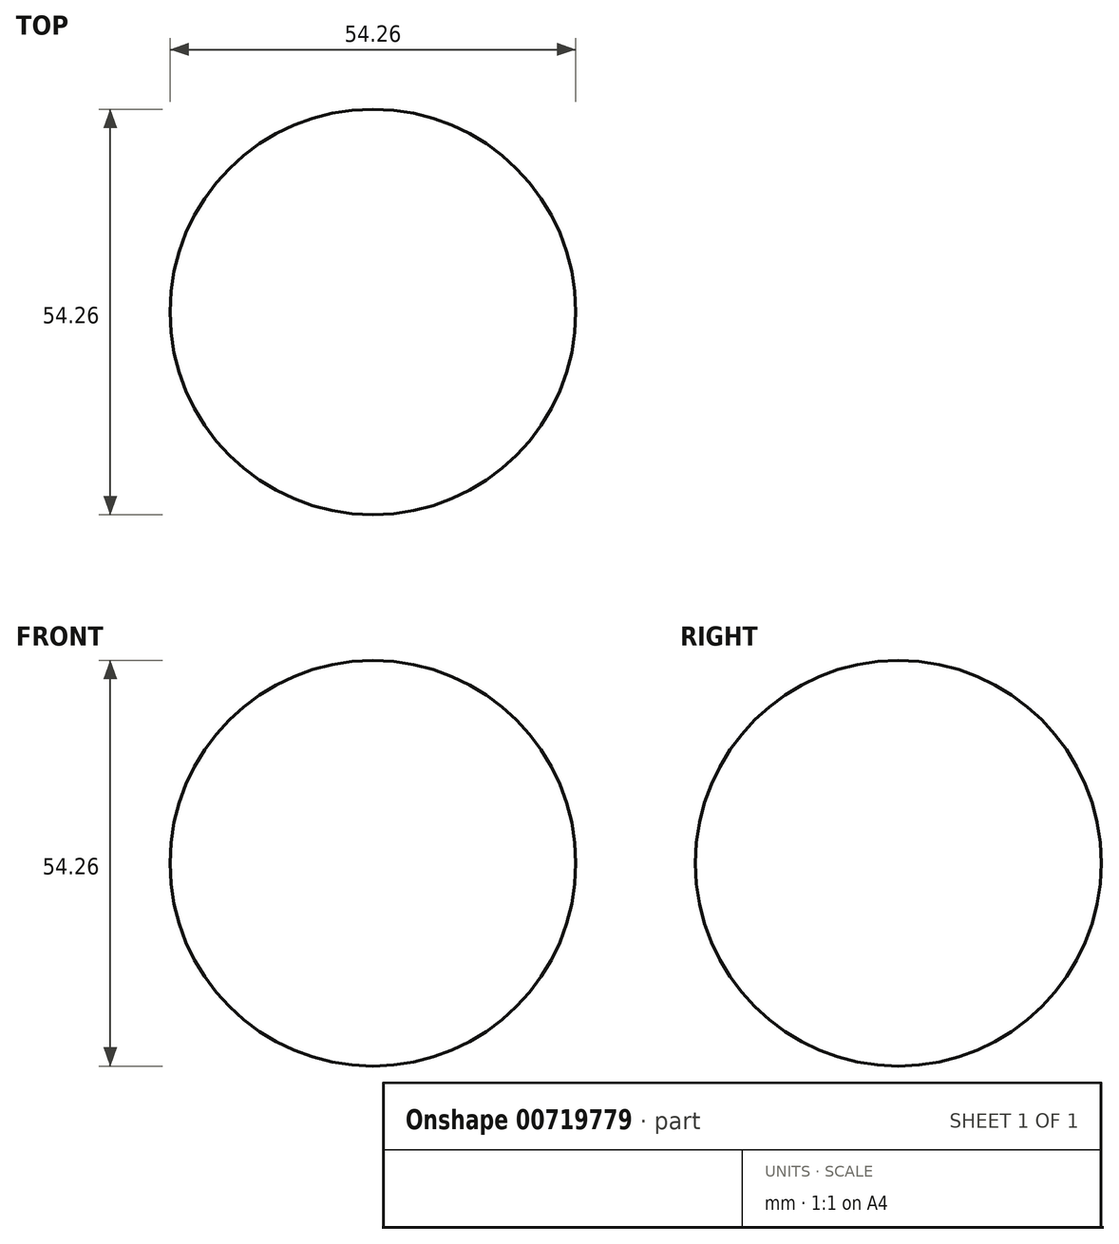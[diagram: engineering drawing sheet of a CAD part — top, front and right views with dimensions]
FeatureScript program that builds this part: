
annotation { "Feature Type Name" : "Feature", "Feature Type Description" : "" }
export const myFeature = defineFeature(function(context is Context, id is Id, definition is map)
    precondition{}
    {
        {
            var Q0;
            Q0=qCreatedBy(makeId("Front.planeOp"),FACE);
            var sketch = newSketch(context, id + "F0", { "sketchPlane" : qUnion([Q0])});
            skArc(sketch, "E0", {"start": v(27.13, 0) * mm, "mid": v(0, 27.13) * mm, "end": v(-27.13, 0) * mm});
            skLineSegment(sketch, "E1", {"start": v(-27.13, 0) * mm, "end": v(27.13, 0) * mm});
            skSolve(sketch);
        }
        {
            var Q0;
            Q0=sQuery(id+"F0.wireOp",EDGE,"E0");
            var Q1;
            Q1=sQuery(id+"F0.wireOp",EDGE,"E1");
            revolve(context, id + "F1", {"bodyType" : ToolBodyType.SURFACE, "surfaceOperationType" : NewSurfaceOperationType.NEW, "surfaceEntities" : qUnion([Q0]), "axis" : qUnion([Q1]), "revolveType" : RevolveType.FULL});
        }
    });
